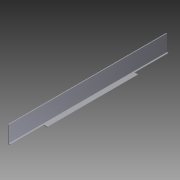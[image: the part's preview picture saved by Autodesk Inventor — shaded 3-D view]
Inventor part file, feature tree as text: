
AUTODESK INVENTOR PART (.ipt)
format: ipt  version: 2012 (Build 160160000, 160)  size: 88,064 bytes
history: native  units: in
note: dims shown in document units (in); Inventor stores cm internally (conversion verified against a paired STEP export)
features: extrude x2, sketch x2
ambient origin geometry x8: Origin, YZ Plane, XZ Plane, XY Plane, X Axis, Y Axis, Z Axis, Center Point
bodies: Solid1 (feature_tree)
feature tree (4):
  extrude  "Extrusion1"  Depth=1.0in
  extrude  "Extrusion2"  Depth=0.125in
  sketch  "Sketch1"  dims[d0=3.0in d1=1.0in]
  sketch  "Sketch2"  dims[d2=0.125in d3=0.125in d4=28.0in d5=0.0in d7=0.625in d8=6.0in d9=1.0in d10=0.0in]
